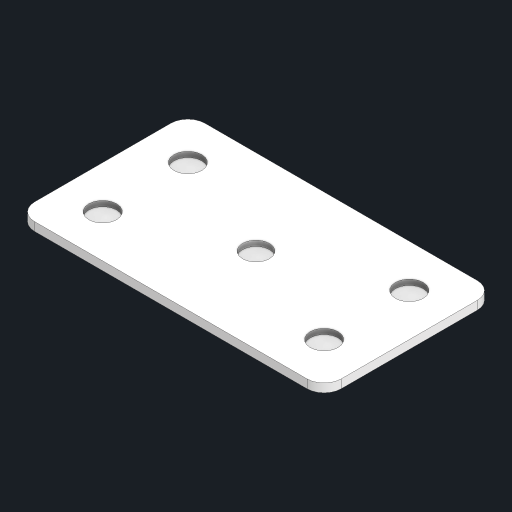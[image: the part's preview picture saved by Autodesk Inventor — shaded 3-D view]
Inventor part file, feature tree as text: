
AUTODESK INVENTOR PART (.ipt)
format: ipt  version: 2024 (Build 280153000, 153)  size: 146,432 bytes
history: native  units: in
note: dims shown in document units (in); Inventor stores cm internally (conversion verified against a paired STEP export)
features: extrude x1, sketch x1, projected_geometry x1
ambient origin geometry x8: Origin, YZ Plane, XZ Plane, XY Plane, X Axis, Y Axis, Z Axis, Center Point
bodies: Solid1 (feature_tree), Body1 (feature_tree)
feature tree (3):
  extrude  "Extrusion2"  Depth=0.0787in
  sketch  "Sketch2"  dims[d2=0.007in d3=0.007in d4=0.007in d5=0.007in d6=0.007in d7=0.0787in d8=0.0in]
  projected_geometry  "Projected Loop2"
